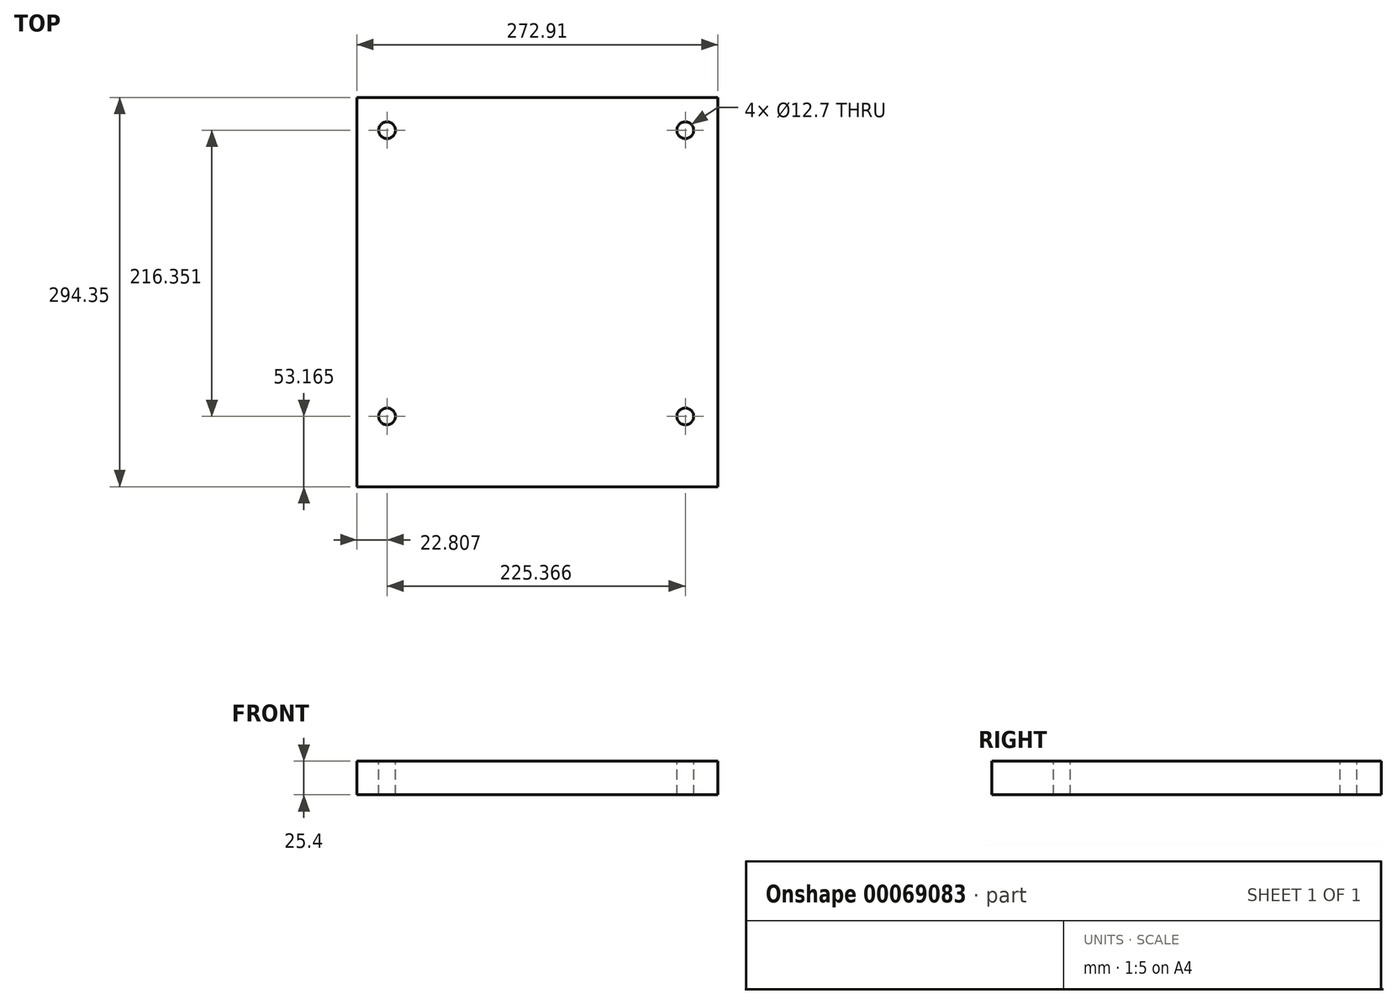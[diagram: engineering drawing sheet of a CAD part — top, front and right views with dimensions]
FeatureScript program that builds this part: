
annotation { "Feature Type Name" : "Feature", "Feature Type Description" : "" }
export const myFeature = defineFeature(function(context is Context, id is Id, definition is map)
    precondition{}
    {
        {
            var Q0;
            Q0=qCreatedBy(makeId("Top.planeOp"),FACE);
            var sketch = newSketch(context, id + "F0", { "sketchPlane" : qUnion([Q0])});
            skLineSegment(sketch, "E0.bottom", {"start": v(-170.79, 141.88) * mm, "end": v(102.12, 141.88) * mm});
            skLineSegment(sketch, "E0.top", {"start": v(-170.79, -152.47) * mm, "end": v(102.12, -152.47) * mm});
            skLineSegment(sketch, "E0.left", {"start": v(-170.79, 141.88) * mm, "end": v(-170.79, -152.47) * mm});
            skLineSegment(sketch, "E0.right", {"start": v(102.12, 141.88) * mm, "end": v(102.12, -152.47) * mm});
            skSolve(sketch);
        }
        {
            var Q0;
            Q0=makeQuery(id+"F0.imprint","IMPRINT",FACE,{"disambiguationData":[TD([[makeQuery(id+"F0.imprint","IMPRINT",EDGE,{"derivedFrom":sQuery(id+"F0.wireOp",EDGE,"E0.bottom")}),-1.0]])]});
            extrude(context, id + "F1", {"entities" : qUnion([Q0]), "depth" : 25.4 * mm});
        }
        {
            var Q0;
            Q0=makeQuery(id+"F1.opExtrude","CAP_FACE",FACE,{"disambiguationData":[OSD([sQuery(id+"F0.wireOp",EDGE,"E0.bottom"),sQuery(id+"F0.wireOp",EDGE,"E0.top"),sQuery(id+"F0.wireOp",EDGE,"E0.left"),sQuery(id+"F0.wireOp",EDGE,"E0.right")])],"isStart":false});
            var sketch = newSketch(context, id + "F2", { "sketchPlane" : qUnion([Q0])});
            skLineSegment(sketch, "E1.rect.bottom", {"start": v(77.38, -99.3) * mm, "end": v(-147.98, -99.3) * mm});
            skLineSegment(sketch, "E1.rect.top", {"start": v(77.38, 117.05) * mm, "end": v(-147.98, 117.05) * mm});
            skLineSegment(sketch, "E1.rect.left", {"start": v(77.38, -99.3) * mm, "end": v(77.38, 117.05) * mm});
            skLineSegment(sketch, "E1.rect.right", {"start": v(-147.98, -99.3) * mm, "end": v(-147.98, 117.05) * mm});
            skPoint(sketch, "E1.rect.middle", {"position": v(-35.3, 8.87) * mm});
            skSolve(sketch);
        }
        {
            var Q0;
            Q0=sQuery(id+"F2.wireOp",VERTEX,"E1.rect.top.end");
            var Q1;
            Q1=sQuery(id+"F2.wireOp",VERTEX,"E1.rect.left.end");
            var Q2;
            Q2=sQuery(id+"F2.wireOp",VERTEX,"E1.rect.right.start");
            var Q3;
            Q3=sQuery(id+"F2.wireOp",VERTEX,"E1.rect.left.start");
            var Q4;
            Q4=makeQuery(id+"F1.opExtrude","SWEPT_BODY",BODY,{"disambiguationData":[OSD([sQuery(id+"F0.wireOp",EDGE,"E0.bottom"),sQuery(id+"F0.wireOp",EDGE,"E0.top"),sQuery(id+"F0.wireOp",EDGE,"E0.left"),sQuery(id+"F0.wireOp",EDGE,"E0.right")])]});
            hole(context, id + "F3", {"style" : HoleStyle.SIMPLE, "holeDiameter" : 12.7 * mm, "endStyle" : HoleEndStyle.THROUGH, "locations" : qUnion([Q0, Q1, Q2, Q3]), "scope" : qUnion([Q4])});
        }
    });
